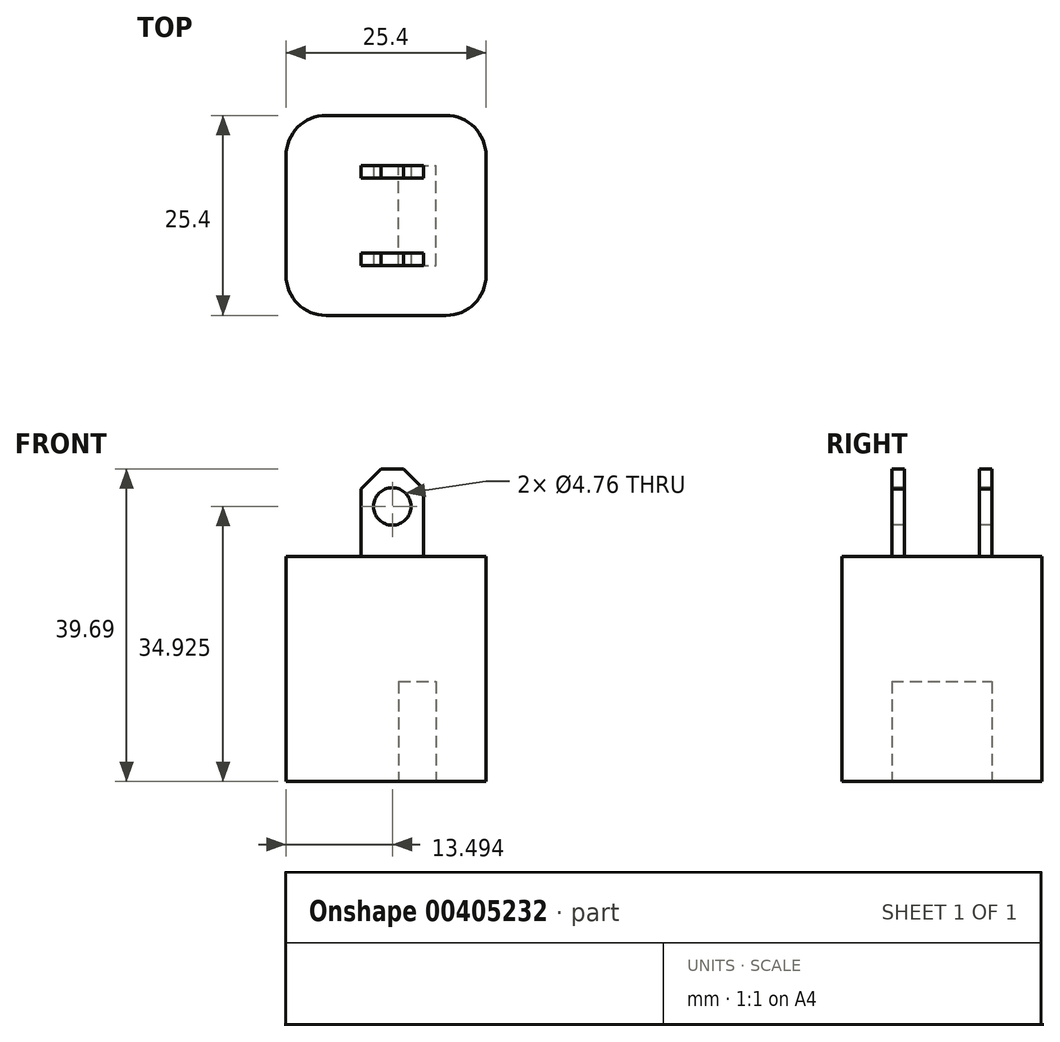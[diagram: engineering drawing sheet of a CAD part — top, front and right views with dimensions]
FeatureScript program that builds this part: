
annotation { "Feature Type Name" : "Feature", "Feature Type Description" : "" }
export const myFeature = defineFeature(function(context is Context, id is Id, definition is map)
    precondition{}
    {
        {
            var Q0;
            Q0=qCreatedBy(makeId("Top.planeOp"),FACE);
            var sketch = newSketch(context, id + "F0", { "sketchPlane" : qUnion([Q0])});
            skLineSegment(sketch, "E0.bottom", {"start": v(0, 0) * mm, "end": v(-25.4, 0) * mm});
            skLineSegment(sketch, "E0.top", {"start": v(0, 25.4) * mm, "end": v(-25.4, 25.4) * mm});
            skLineSegment(sketch, "E0.left", {"start": v(0, 0) * mm, "end": v(0, 25.4) * mm});
            skLineSegment(sketch, "E0.right", {"start": v(-25.4, 0) * mm, "end": v(-25.4, 25.4) * mm});
            skSolve(sketch);
        }
        {
            var Q0;
            Q0=makeQuery(id+"F0.imprint","IMPRINT",FACE,{"disambiguationData":[TD([[makeQuery(id+"F0.imprint","IMPRINT",EDGE,{"derivedFrom":sQuery(id+"F0.wireOp",EDGE,"E0.bottom")}),-1.0]])]});
            extrude(context, id + "F1", {"entities" : qUnion([Q0]), "depth" : 28.57 * mm});
        }
        {
            var Q0;
            Q0=makeQuery(id+"F1.opExtrude","CAP_FACE",FACE,{"disambiguationData":[OSD([sQuery(id+"F0.wireOp",EDGE,"E0.bottom"),sQuery(id+"F0.wireOp",EDGE,"E0.top"),sQuery(id+"F0.wireOp",EDGE,"E0.left"),sQuery(id+"F0.wireOp",EDGE,"E0.right")])],"isStart":false});
            var sketch = newSketch(context, id + "F2", { "sketchPlane" : qUnion([Q0])});
            skLineSegment(sketch, "E1.bottom", {"start": v(-15.88, 19.05) * mm, "end": v(-7.94, 19.05) * mm});
            skLineSegment(sketch, "E1.top", {"start": v(-15.88, 17.46) * mm, "end": v(-7.94, 17.46) * mm});
            skLineSegment(sketch, "E1.left", {"start": v(-15.88, 19.05) * mm, "end": v(-15.88, 17.46) * mm});
            skLineSegment(sketch, "E1.right", {"start": v(-7.94, 19.05) * mm, "end": v(-7.94, 17.46) * mm});
            skLineSegment(sketch, "E2.bottom", {"start": v(-15.88, 7.94) * mm, "end": v(-7.94, 7.94) * mm});
            skLineSegment(sketch, "E2.top", {"start": v(-15.88, 6.35) * mm, "end": v(-7.94, 6.35) * mm});
            skLineSegment(sketch, "E2.left", {"start": v(-15.88, 7.94) * mm, "end": v(-15.88, 6.35) * mm});
            skLineSegment(sketch, "E2.right", {"start": v(-7.94, 7.94) * mm, "end": v(-7.94, 6.35) * mm});
            skSolve(sketch);
        }
        {
            var Q0;
            Q0=makeQuery(id+"F2.imprint","IMPRINT",FACE,{"disambiguationData":[TD([[makeQuery(id+"F2.imprint","IMPRINT",EDGE,{"derivedFrom":sQuery(id+"F2.wireOp",EDGE,"E2.bottom")}),-1.0]])]});
            var Q1;
            Q1=makeQuery(id+"F2.imprint","IMPRINT",FACE,{"disambiguationData":[TD([[makeQuery(id+"F2.imprint","IMPRINT",EDGE,{"derivedFrom":sQuery(id+"F2.wireOp",EDGE,"E1.bottom")}),-1.0]])]});
            extrude(context, id + "F3", {"entities" : qUnion([Q0, Q1]), "operationType" : NewBodyOperationType.ADD, "depth" : 11.1 * mm});
        }
        {
            var Q0;
            Q0=makeQuery(id+"F3.opExtrude","SWEPT_FACE",FACE,{"disambiguationData":[OSD([sQuery(id+"F2.wireOp",EDGE,"E2.top")])]});
            var sketch = newSketch(context, id + "F4", { "sketchPlane" : qUnion([Q0])});
            skCircle(sketch, "E3", {"center": v(-11.9, 34.92) * mm, "radius": 2.38 * mm});
            skSolve(sketch);
        }
        {
            var Q0;
            Q0=makeQuery(id+"F4.imprint","IMPRINT",FACE,{"disambiguationData":[TD([[makeQuery(id+"F4.imprint","IMPRINT",EDGE,{"derivedFrom":sQuery(id+"F4.wireOp",EDGE,"E3")}),1.0]])]});
            extrude(context, id + "F5", {"entities" : qUnion([Q0]), "operationType" : NewBodyOperationType.REMOVE, "oppositeDirection" : true, "depth" : 12.95 * mm});
        }
        {
            var Q0;
            Q0=makeQuery(id+"F1.opExtrude","SWEPT_EDGE",EDGE,{"disambiguationData":[OSD([sQuery(id+"F0.wireOp",EDGE,"E0.top"),sQuery(id+"F0.wireOp",EDGE,"E0.left")])]});
            var Q1;
            Q1=makeQuery(id+"F1.opExtrude","SWEPT_EDGE",EDGE,{"disambiguationData":[OSD([sQuery(id+"F0.wireOp",EDGE,"E0.bottom"),sQuery(id+"F0.wireOp",EDGE,"E0.left")])]});
            var Q2;
            Q2=makeQuery(id+"F1.opExtrude","SWEPT_EDGE",EDGE,{"disambiguationData":[OSD([sQuery(id+"F0.wireOp",EDGE,"E0.bottom"),sQuery(id+"F0.wireOp",EDGE,"E0.right")])]});
            var Q3;
            Q3=makeQuery(id+"F1.opExtrude","SWEPT_EDGE",EDGE,{"disambiguationData":[OSD([sQuery(id+"F0.wireOp",EDGE,"E0.top"),sQuery(id+"F0.wireOp",EDGE,"E0.right")])]});
            fillet(context, id + "F6", {"entities" : qUnion([Q0, Q1, Q2, Q3]), "radius" : 5.08 * mm, "tangentPropagation" : true, "allowEdgeOverflow" : false});
        }
        {
            var Q0;
            Q0=makeQuery(id+"F3.opExtrude","CAP_EDGE",EDGE,{"disambiguationData":[OSD([sQuery(id+"F2.wireOp",EDGE,"E1.left")])],"isStart":false});
            var Q1;
            Q1=makeQuery(id+"F3.opExtrude","CAP_EDGE",EDGE,{"disambiguationData":[OSD([sQuery(id+"F2.wireOp",EDGE,"E1.right")])],"isStart":false});
            var Q2;
            Q2=makeQuery(id+"F3.opExtrude","CAP_EDGE",EDGE,{"disambiguationData":[OSD([sQuery(id+"F2.wireOp",EDGE,"E2.right")])],"isStart":false});
            var Q3;
            Q3=makeQuery(id+"F3.opExtrude","CAP_EDGE",EDGE,{"disambiguationData":[OSD([sQuery(id+"F2.wireOp",EDGE,"E2.left")])],"isStart":false});
            chamfer(context, id + "F7", {"entities" : qUnion([Q0, Q1, Q2, Q3]), "width" : 2.54 * mm, "tangentPropagation" : true});
        }
        {
            var Q0;
            Q0=makeQuery(id+"F1.opExtrude","CAP_FACE",FACE,{"disambiguationData":[OSD([sQuery(id+"F0.wireOp",EDGE,"E0.bottom"),sQuery(id+"F0.wireOp",EDGE,"E0.top"),sQuery(id+"F0.wireOp",EDGE,"E0.left"),sQuery(id+"F0.wireOp",EDGE,"E0.right")])],"isStart":true});
            var sketch = newSketch(context, id + "F8", { "sketchPlane" : qUnion([Q0])});
            skLineSegment(sketch, "E4.bottom", {"start": v(-11.11, -6.35) * mm, "end": v(-6.35, -6.35) * mm});
            skLineSegment(sketch, "E4.top", {"start": v(-11.11, -19.05) * mm, "end": v(-6.35, -19.05) * mm});
            skLineSegment(sketch, "E4.left", {"start": v(-11.11, -6.35) * mm, "end": v(-11.11, -19.05) * mm});
            skLineSegment(sketch, "E4.right", {"start": v(-6.35, -6.35) * mm, "end": v(-6.35, -19.05) * mm});
            skSolve(sketch);
        }
        {
            var Q0;
            Q0=makeQuery(id+"F8.imprint","IMPRINT",FACE,{"disambiguationData":[TD([[makeQuery(id+"F8.imprint","IMPRINT",EDGE,{"derivedFrom":sQuery(id+"F8.wireOp",EDGE,"E4.bottom")}),-1.0]])]});
            extrude(context, id + "F9", {"entities" : qUnion([Q0]), "operationType" : NewBodyOperationType.REMOVE, "oppositeDirection" : true, "depth" : 12.7 * mm});
        }
    });
